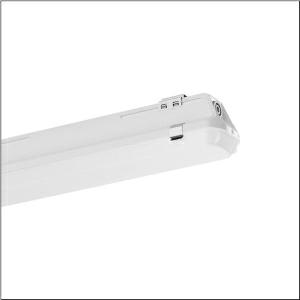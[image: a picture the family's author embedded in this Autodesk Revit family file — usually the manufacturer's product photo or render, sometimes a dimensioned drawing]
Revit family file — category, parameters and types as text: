
# Revit family: monsun_r__11_emergency_51fp207p437h3g_0ff0
name_source: partatom
category: Lighting Fixtures
units: mm (PartAtom-declared; Revit-internal decimal feet)

## family parameters
Cut with Voids When Loaded = No
Host = Face
Light Source = No
Part Type = Normal
Room Calculation Point = No
Round Connector Dimension = Use Diameter
Shared = No

## types (1)
- Monsun® 11 emergency (1 x LED, 3990 lm, 27.5 W, 4000K)
    Apparent Load = 28 VA
    CIE Flux Codes = 45 75 93 94 100
    Color Rendering = 80
    Color Temperature = 4000K
    Default Elevation = 1800 mm
    Description = Monsun® 11 emergency, damp-proof luminaire, chain hanger, primary optical cover: enclosure, of PC, light emission: direct distribution, primary light characteristic: symmetric, installation type: suspended mounting, surface-mounted, horizontal mounting, vertical mounting, LED, rated luminous flux: 3.990lm, luminous efficacy: 145lm/W, light colour: 840, colour temperature: 4000K, control gear: ECG, with terminal, 4-pole, max. 2.5mm², mains connection: 220..240V, AC, 50/60Hz, rated input power: 28W, control gear: single battery element, battery: NiCd, 4,5Ah, mains connection: 230V, luminaire housing, of glass-fibre reinforced polyester, uncoated, bright grey, incl. chain hanger, length: 1.590mm, width: 90mm, height: 88mm, clip for enclosure, of stainless steel (V2A), ceiling mounting element, of stainless steel (V2A), chain hanger, of stainless steel (V2A), protection rating (complete): IP66, insulation class (complete): insulation class I (protective earthing), certification: CE, UKCA, protection symbol: D, impact resistance: IK08, permissible operating ambient temperature: +5..+35°C, standard: EN 50419, EN 60598-2-1, EN 60598-2-22, no direct snow, no direct sun, no direct rain, for indoor or canopied outdoor use, corresponds to IFS (International Featured Standards) requirements for safety and quality in the food industry, contact your sales advisor before using the luminaires in applications with unclear chemical exposure, large temperature fluctuations or condensation-forming humidity, LABS conformity tested according to VDMA 24364:2018-05, packaging unit: 1 piece
    Height = 89 mm
    Lamp = 1 x LED
    Lamp Light Flux = 3990 lm
    Lamp Power = 27.5 W
    Lamp count = 1
    Length = 1590 mm
    Luminous efficacy = 145 lm/W
    Manufacturer = Siteco
    ModVariant = No
    Model = 51FP207P437H3G
    Mounting Place = Ceiling
    Mounting Type = Surface mounted
    Number of Poles = 1
    OnlyDefault = Yes
    Power Factor = 1
    Product Name = Monsun® 11 emergency
    Product group = damp-proof luminaire
    ProductGroupID = 301
    Protection Class = Protection class I
    Protection Degree = IP 66
    RLX_Detail_Level = 1
    RLX_Emergency_Light_Flux = 0 lm
    RLX_Emergency_Type = 0
    RLX_Emergency_Type_DB = No
    RlxData = <blob elided: 89025 chars, md5=f1979548>
    Socket = socket
    Standby Power = 0 W
    System Light Flux = 3990 lm
    System Power = 28 W
    Type Comments = Product without accessories
    Type Image = l_1004748.jpg
    URL = http://relux.com
    VarID = ---
    Voltage = 0 V
    Weight = 0.00 kg
    Width = 90 mm

## geometry (parser evidence)
native form markers: Blend x4, Sweep x13
no freeform markers — native parametric forms only
